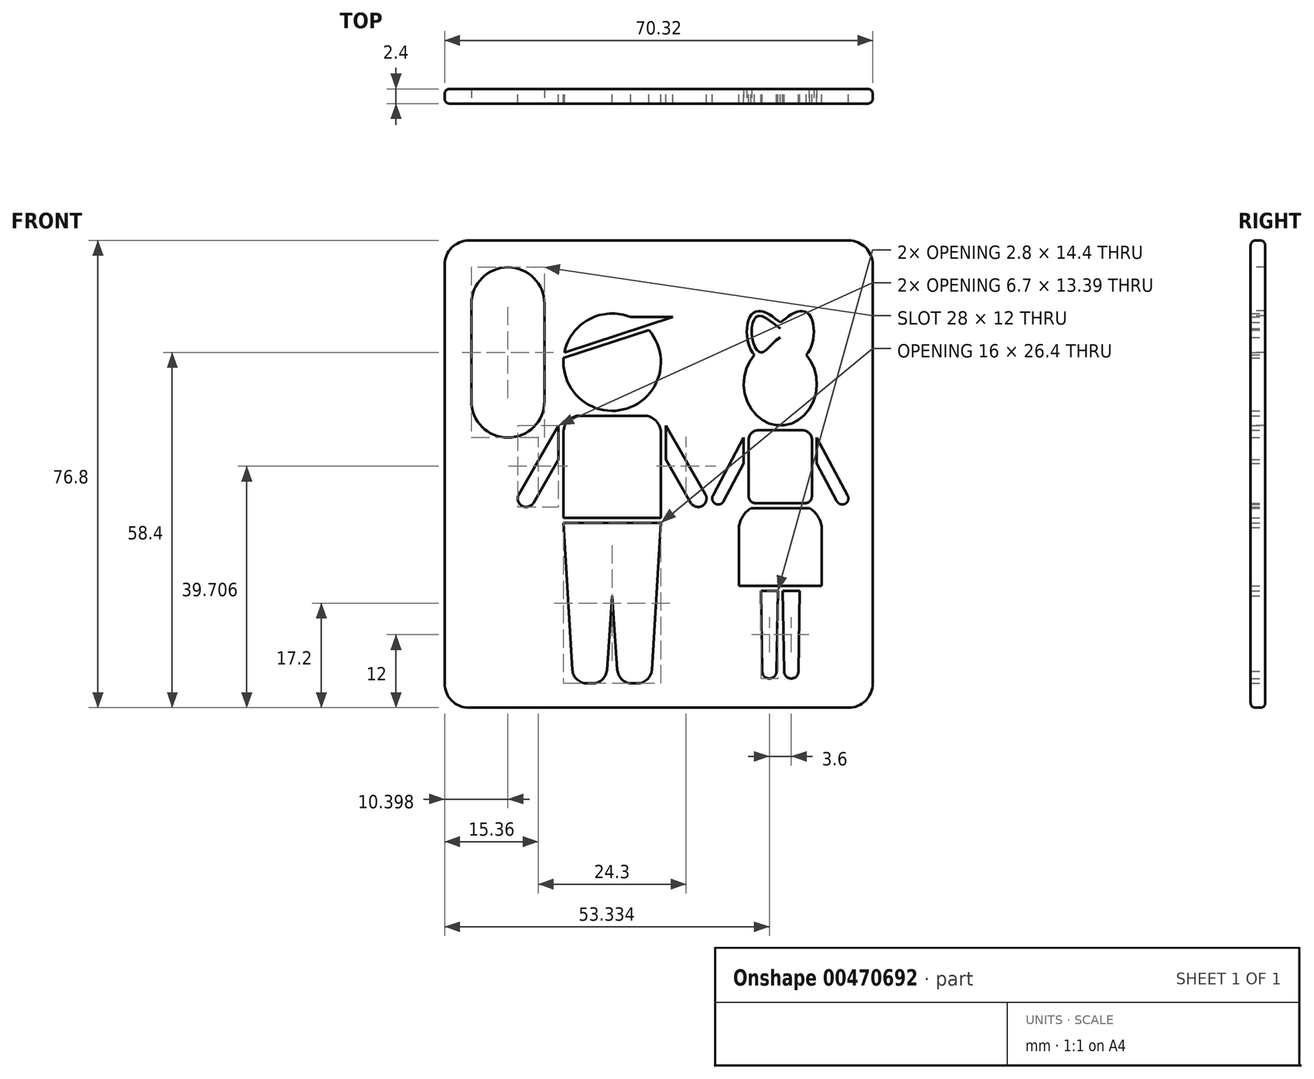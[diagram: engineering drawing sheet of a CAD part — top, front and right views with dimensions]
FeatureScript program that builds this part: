
annotation { "Feature Type Name" : "Feature", "Feature Type Description" : "" }
export const myFeature = defineFeature(function(context is Context, id is Id, definition is map)
    precondition{}
    {
        {
            var Q0;
            Q0=qCreatedBy(makeId("Front.planeOp"),FACE);
            var sketch = newSketch(context, id + "F0", { "sketchPlane" : qUnion([Q0])});
            skLineSegment(sketch, "E0", {"start": v(-25, 66) * mm, "end": v(-25, 0) * mm, "construction": true});
            skArc(sketch, "E1", {"start": v(-21.19, 75.25) * mm, "mid": v(-29.7, 74.83) * mm, "end": v(-34.8, 68) * mm});
            skLineSegment(sketch, "E2.bottom", {"start": v(-31.5, 55) * mm, "end": v(-18.5, 55) * mm});
            skLineSegment(sketch, "E2.top", {"start": v(-35, 34) * mm, "end": v(-15, 34) * mm});
            skLineSegment(sketch, "E2.left", {"start": v(-35, 51.5) * mm, "end": v(-35, 34) * mm});
            skLineSegment(sketch, "E2.right", {"start": v(-15, 51.5) * mm, "end": v(-15, 34) * mm});
            skPoint(sketch, "E2.middle", {"position": v(-25, 44.5) * mm});
            skPoint(sketch, "E3.visualSharp", {"position": v(-15, 55) * mm});
            skArc(sketch, "E3.filletArc", {"start": v(-15, 51.5) * mm, "mid": v(-16.03, 53.97) * mm, "end": v(-18.5, 55) * mm});
            skPoint(sketch, "E4.visualSharp", {"position": v(-35, 55) * mm});
            skArc(sketch, "E4.filletArc", {"start": v(-31.5, 55) * mm, "mid": v(-33.97, 53.97) * mm, "end": v(-35, 51.5) * mm});
            skLineSegment(sketch, "E5", {"start": v(-35, 66) * mm, "end": v(-15, 66) * mm, "construction": true});
            skLineSegment(sketch, "E6", {"start": v(-34.8, 68) * mm, "end": v(-12.5, 75.25) * mm});
            skLineSegment(sketch, "E7", {"start": v(-12.5, 75.25) * mm, "end": v(-21.19, 75.25) * mm});
            skLineSegment(sketch, "E8", {"start": v(-34.96, 66.9) * mm, "end": v(-17.47, 72.58) * mm});
            skLineSegment(sketch, "E9", {"start": v(-35, 33) * mm, "end": v(-15, 33) * mm});
            skLineSegment(sketch, "E10", {"start": v(-35, 33) * mm, "end": v(-33.15, 2.82) * mm});
            skLineSegment(sketch, "E11", {"start": v(-30.16, 0) * mm, "end": v(-29.06, 0) * mm});
            skLineSegment(sketch, "E12", {"start": v(-26.06, 2.8) * mm, "end": v(-25, 18) * mm});
            skPoint(sketch, "E13.visualSharp", {"position": v(-26.26, 0) * mm});
            skArc(sketch, "E13.filletArc", {"start": v(-29.06, 0) * mm, "mid": v(-27.01, 0.8) * mm, "end": v(-26.06, 2.8) * mm});
            skPoint(sketch, "E14.visualSharp", {"position": v(-32.98, 0) * mm});
            skArc(sketch, "E14.filletArc", {"start": v(-33.15, 2.82) * mm, "mid": v(-32.22, 0.81) * mm, "end": v(-30.16, 0) * mm});
            skLineSegment(sketch, "E15.MirrorCS", {"start": v(-15, 33) * mm, "end": v(-16.85, 2.82) * mm});
            skArc(sketch, "E16.MirrorCS", {"start": v(-16.85, 2.82) * mm, "mid": v(-17.78, 0.81) * mm, "end": v(-19.84, 0) * mm});
            skLineSegment(sketch, "E17.MirrorCS", {"start": v(-19.84, 0) * mm, "end": v(-20.94, 0) * mm});
            skArc(sketch, "E18.MirrorCS", {"start": v(-20.94, 0) * mm, "mid": v(-22.99, 0.8) * mm, "end": v(-23.94, 2.8) * mm});
            skLineSegment(sketch, "E19.MirrorCS", {"start": v(-23.94, 2.8) * mm, "end": v(-25, 18) * mm});
            skLineSegment(sketch, "E20", {"start": v(-36, 53) * mm, "end": v(-44.16, 38.88) * mm});
            skLineSegment(sketch, "E21", {"start": v(-41.12, 37.13) * mm, "end": v(-36, 46) * mm});
            skLineSegment(sketch, "E22", {"start": v(-36, 46) * mm, "end": v(-36, 53) * mm});
            skArc(sketch, "E23", {"start": v(-44.16, 38.88) * mm, "mid": v(-43.51, 36.48) * mm, "end": v(-41.12, 37.13) * mm});
            skLineSegment(sketch, "E24.MirrorCS", {"start": v(-14, 53) * mm, "end": v(-5.84, 38.88) * mm});
            skLineSegment(sketch, "E25.MirrorCS", {"start": v(-8.88, 37.13) * mm, "end": v(-14, 46) * mm});
            skLineSegment(sketch, "E26.MirrorCS", {"start": v(-14, 46) * mm, "end": v(-14, 53) * mm});
            skArc(sketch, "E27.MirrorCS", {"start": v(-5.84, 38.88) * mm, "mid": v(-6.49, 36.48) * mm, "end": v(-8.88, 37.13) * mm});
            skArc(sketch, "E28.trimOffspring", {"start": v(-34.96, 66.9) * mm, "mid": v(-21.9, 56.49) * mm, "end": v(-17.47, 72.58) * mm});
            skLineSegment(sketch, "E29", {"start": v(9.53, 1) * mm, "end": v(9.53, 61.5) * mm, "construction": true});
            skLineSegment(sketch, "E30.bottom", {"start": v(5.53, 19) * mm, "end": v(9.03, 19) * mm});
            skLineSegment(sketch, "E30.top", {"start": v(5.82, 2.46) * mm, "end": v(8.74, 2.46) * mm, "construction": true});
            skLineSegment(sketch, "E30.left", {"start": v(5.53, 19) * mm, "end": v(5.82, 2.46) * mm});
            skLineSegment(sketch, "E30.right", {"start": v(9.03, 19) * mm, "end": v(8.74, 2.46) * mm});
            skArc(sketch, "E31", {"start": v(8.74, 2.46) * mm, "mid": v(7.28, 1) * mm, "end": v(5.82, 2.46) * mm});
            skLineSegment(sketch, "E32", {"start": v(5.17, 1) * mm, "end": v(7.83, 1) * mm, "construction": true});
            skLineSegment(sketch, "E33", {"start": v(9.53, 20) * mm, "end": v(1.03, 20) * mm});
            skLineSegment(sketch, "E34", {"start": v(1.03, 20) * mm, "end": v(1.03, 32) * mm});
            skLineSegment(sketch, "E35", {"start": v(9.53, 36) * mm, "end": v(3.53, 36) * mm});
            skArc(sketch, "E36", {"start": v(3.53, 36) * mm, "mid": v(1.8, 34.3) * mm, "end": v(1.03, 32) * mm});
            skLineSegment(sketch, "E37.MirrorCS", {"start": v(13.24, 2.46) * mm, "end": v(10.32, 2.46) * mm, "construction": true});
            skArc(sketch, "E38.MirrorCS", {"start": v(10.32, 2.46) * mm, "mid": v(11.78, 1) * mm, "end": v(13.24, 2.46) * mm});
            skLineSegment(sketch, "E39.MirrorCS", {"start": v(10.03, 19) * mm, "end": v(10.32, 2.46) * mm});
            skLineSegment(sketch, "E40.MirrorCS", {"start": v(13.53, 19) * mm, "end": v(10.03, 19) * mm});
            skLineSegment(sketch, "E41.MirrorCS", {"start": v(13.53, 19) * mm, "end": v(13.24, 2.46) * mm});
            skLineSegment(sketch, "E42.MirrorCS", {"start": v(9.53, 36) * mm, "end": v(15.53, 36) * mm});
            skArc(sketch, "E43.MirrorCS", {"start": v(15.53, 36) * mm, "mid": v(17.26, 34.3) * mm, "end": v(18.03, 32) * mm});
            skLineSegment(sketch, "E44.MirrorCS", {"start": v(18.03, 20) * mm, "end": v(18.03, 32) * mm});
            skLineSegment(sketch, "E45.MirrorCS", {"start": v(9.53, 20) * mm, "end": v(18.03, 20) * mm});
            skLineSegment(sketch, "E46", {"start": v(9.53, 37) * mm, "end": v(4.53, 37) * mm});
            skLineSegment(sketch, "E47", {"start": v(3.03, 38.5) * mm, "end": v(3.03, 50) * mm});
            skLineSegment(sketch, "E48", {"start": v(5.03, 52) * mm, "end": v(9.53, 52) * mm});
            skPoint(sketch, "E49.visualSharp", {"position": v(3.03, 37) * mm});
            skArc(sketch, "E49.filletArc", {"start": v(3.03, 38.5) * mm, "mid": v(3.47, 37.44) * mm, "end": v(4.53, 37) * mm});
            skPoint(sketch, "E50.visualSharp", {"position": v(3.03, 52) * mm});
            skArc(sketch, "E50.filletArc", {"start": v(5.03, 52) * mm, "mid": v(3.62, 51.41) * mm, "end": v(3.03, 50) * mm});
            skLineSegment(sketch, "E51.MirrorCS", {"start": v(14.03, 52) * mm, "end": v(9.53, 52) * mm});
            skArc(sketch, "E52.MirrorCS", {"start": v(14.03, 52) * mm, "mid": v(15.44, 51.41) * mm, "end": v(16.03, 50) * mm});
            skLineSegment(sketch, "E53.MirrorCS", {"start": v(16.03, 38.5) * mm, "end": v(16.03, 50) * mm});
            skArc(sketch, "E54.MirrorCS", {"start": v(16.03, 38.5) * mm, "mid": v(15.6, 37.44) * mm, "end": v(14.53, 37) * mm});
            skLineSegment(sketch, "E55.MirrorCS", {"start": v(9.53, 37) * mm, "end": v(14.53, 37) * mm});
            skLineSegment(sketch, "E56", {"start": v(2.03, 50.5) * mm, "end": v(2.03, 45.17) * mm});
            skLineSegment(sketch, "E57", {"start": v(2.03, 45.17) * mm, "end": v(-2.1, 37.41) * mm});
            skLineSegment(sketch, "E58", {"start": v(-2.1, 37.41) * mm, "end": v(-4.3, 38.59) * mm, "construction": true});
            skLineSegment(sketch, "E59", {"start": v(-4.3, 38.59) * mm, "end": v(2.03, 50.5) * mm});
            skArc(sketch, "E60", {"start": v(-2.1, 37.41) * mm, "mid": v(-3.79, 36.9) * mm, "end": v(-4.3, 38.59) * mm});
            skLineSegment(sketch, "E61.MirrorCS", {"start": v(17.03, 50.5) * mm, "end": v(17.03, 45.17) * mm});
            skLineSegment(sketch, "E62.MirrorCS", {"start": v(23.36, 38.59) * mm, "end": v(17.03, 50.5) * mm});
            skLineSegment(sketch, "E63.MirrorCS", {"start": v(17.03, 45.17) * mm, "end": v(21.16, 37.41) * mm});
            skArc(sketch, "E64.MirrorCS", {"start": v(21.16, 37.41) * mm, "mid": v(22.85, 36.9) * mm, "end": v(23.36, 38.59) * mm});
            skEllipticalArc(sketch, "E65", {});
            skPoint(sketch, "E66.4.internal.snap0", {"position": v(9.53, 70) * mm});
            skFitSpline(sketch, "E66", {"points": [v(9.53, 71.09) * mm, v(5.61, 67.97) * mm, v(3.73, 71.18) * mm, v(5.07, 75.5) * mm, v(9.53, 72.94) * mm], "startDerivative": vector(-20.3, -12.18) * mm, "endDerivative": vector(11.91, -6.98) * mm});
            skFitSpline(sketch, "E67.MirrorCS", {"points": [v(9.53, 71.09) * mm, v(13.45, 67.97) * mm, v(15.33, 71.18) * mm, v(13.98, 75.5) * mm, v(9.53, 72.94) * mm], "startDerivative": vector(20.3, -12.18) * mm, "endDerivative": vector(-11.91, -6.98) * mm});
            skFitSpline(sketch, "E68.0", {"points": [v(10.04, 70.23) * mm, v(9.7, 70.02) * mm, v(9.2, 69.62) * mm, v(8.55, 69) * mm, v(8.08, 68.52) * mm, v(7.62, 68.05) * mm, v(7.15, 67.62) * mm, v(6.72, 67.3) * mm, v(6.3, 67.1) * mm, v(6, 67) * mm, v(5.73, 66.97) * mm, v(5.44, 66.96) * mm, v(5.1, 67.02) * mm, v(4.74, 67.17) * mm, v(4.33, 67.43) * mm, v(3.92, 67.85) * mm, v(3.54, 68.43) * mm, v(3.23, 69.08) * mm, v(2.99, 69.8) * mm, v(2.8, 70.58) * mm, v(2.7, 71.4) * mm, v(2.65, 72.22) * mm, v(2.68, 73.04) * mm, v(2.79, 73.84) * mm, v(2.98, 74.6) * mm, v(3.28, 75.3) * mm, v(3.66, 75.82) * mm, v(4.08, 76.17) * mm, v(4.46, 76.38) * mm, v(4.83, 76.48) * mm, v(5.12, 76.51) * mm, v(5.4, 76.51) * mm, v(5.75, 76.47) * mm, v(6.25, 76.33) * mm, v(6.82, 76.07) * mm, v(7.48, 75.68) * mm, v(8.11, 75.23) * mm, v(8.7, 74.78) * mm, v(9.25, 74.36) * mm, v(9.72, 74) * mm, v(9.95, 73.85) * mm, v(10.04, 73.8) * mm]});
            skFitSpline(sketch, "E69.0", {"points": [v(9.02, 70.23) * mm, v(9.36, 70.02) * mm, v(9.87, 69.62) * mm, v(10.5, 69) * mm, v(10.98, 68.52) * mm, v(11.44, 68.05) * mm, v(11.9, 67.62) * mm, v(12.34, 67.3) * mm, v(12.76, 67.1) * mm, v(13.06, 67) * mm, v(13.33, 66.97) * mm, v(13.61, 66.96) * mm, v(13.95, 67.02) * mm, v(14.32, 67.17) * mm, v(14.73, 67.43) * mm, v(15.14, 67.85) * mm, v(15.52, 68.43) * mm, v(15.83, 69.08) * mm, v(16.07, 69.8) * mm, v(16.25, 70.58) * mm, v(16.37, 71.4) * mm, v(16.4, 72.22) * mm, v(16.38, 73.04) * mm, v(16.27, 73.84) * mm, v(16.08, 74.6) * mm, v(15.78, 75.3) * mm, v(15.4, 75.82) * mm, v(14.98, 76.17) * mm, v(14.6, 76.38) * mm, v(14.23, 76.48) * mm, v(13.94, 76.51) * mm, v(13.65, 76.51) * mm, v(13.31, 76.47) * mm, v(12.81, 76.33) * mm, v(12.23, 76.07) * mm, v(11.58, 75.68) * mm, v(10.95, 75.23) * mm, v(10.35, 74.78) * mm, v(9.8, 74.36) * mm, v(9.34, 74) * mm, v(9.1, 73.85) * mm, v(9.02, 73.8) * mm]});
            const initialGuessF0  = {"E65": [0.009529412724077696, 0.0615, 0, -1, 0.0085, 0.0075, 3.9233208754425206, 2.359864431737064]};
            skSetInitialGuess(sketch, initialGuessF0);
            skSolve(sketch);
        }
        {
            var Q0;
            Q0=qCreatedBy(makeId("Front.planeOp"),FACE);
            var sketch = newSketch(context, id + "F1", { "sketchPlane" : qUnion([Q0])});
            skLineSegment(sketch, "E70.bottom", {"start": v(-59.39, 91) * mm, "end": v(28.51, 91) * mm});
            skLineSegment(sketch, "E70.top", {"start": v(-59.39, -5) * mm, "end": v(28.51, -5) * mm});
            skLineSegment(sketch, "E70.left", {"start": v(-59.39, 91) * mm, "end": v(-59.39, -5) * mm});
            skLineSegment(sketch, "E70.right", {"start": v(28.51, 91) * mm, "end": v(28.51, -5) * mm});
            skArc(sketch, "E71.0", {"start": v(-44.16, 38.88) * mm, "mid": v(-43.51, 36.48) * mm, "end": v(-41.12, 37.13) * mm, "construction": true});
            skArc(sketch, "E72.0", {"start": v(-21.19, 75.25) * mm, "mid": v(-29.7, 74.83) * mm, "end": v(-34.8, 68) * mm, "construction": true});
            skArc(sketch, "E73.0", {"start": v(21.16, 37.41) * mm, "mid": v(22.85, 36.9) * mm, "end": v(23.36, 38.59) * mm, "construction": true});
            skSolve(sketch);
        }
        {
            var Q0;
            Q0=qSketchRegion(id+"F1",true);
            extrude(context, id + "F2", {"entities" : qUnion([Q0]), "depth" : 3 * mm});
        }
        {
            var Q0;
            Q0=qSketchRegion(id+"F0",true);
            extrude(context, id + "F3", {"entities" : qUnion([Q0]), "operationType" : NewBodyOperationType.REMOVE, "endBound" : BoundingType.THROUGH_ALL, "depth" : 25 * mm});
        }
        {
            var Q0;
            Q0=makeQuery(id+"F2.opExtrude","CAP_FACE",FACE,{"disambiguationData":[OSD([sQuery(id+"F1.wireOp",EDGE,"E70.bottom"),sQuery(id+"F1.wireOp",EDGE,"E70.top"),sQuery(id+"F1.wireOp",EDGE,"E70.left"),sQuery(id+"F1.wireOp",EDGE,"E70.right")])],"isStart":false});
            var sketch = newSketch(context, id + "F4", { "sketchPlane" : qUnion([Q0])});
            skArc(sketch, "E74", {"start": v(-38.89, 78) * mm, "mid": v(-46.39, 85.5) * mm, "end": v(-53.89, 78) * mm});
            skArc(sketch, "E75", {"start": v(-53.89, 58) * mm, "mid": v(-46.39, 50.5) * mm, "end": v(-38.89, 58) * mm});
            skLineSegment(sketch, "E76", {"start": v(-53.89, 78) * mm, "end": v(-53.89, 58) * mm});
            skLineSegment(sketch, "E77", {"start": v(-38.89, 58) * mm, "end": v(-38.89, 78) * mm});
            skSolve(sketch);
        }
        {
            var Q0;
            Q0=makeQuery(id+"F4.imprint","IMPRINT",FACE,{"disambiguationData":[TD([[makeQuery(id+"F4.imprint","IMPRINT",EDGE,{"derivedFrom":sQuery(id+"F4.wireOp",EDGE,"E74")}),1.0]])]});
            extrude(context, id + "F5", {"entities" : qUnion([Q0]), "operationType" : NewBodyOperationType.REMOVE, "endBound" : BoundingType.UP_TO_NEXT, "oppositeDirection" : true, "depth" : 25 * mm, "offsetDistance" : 25 * mm});
        }
        {
            var Q0;
            Q0=makeQuery(id+"F2.opExtrude","SWEPT_EDGE",EDGE,{"disambiguationData":[OSD([sQuery(id+"F1.wireOp",EDGE,"E70.bottom"),sQuery(id+"F1.wireOp",EDGE,"E70.right")])]});
            var Q1;
            Q1=makeQuery(id+"F2.opExtrude","SWEPT_EDGE",EDGE,{"disambiguationData":[OSD([sQuery(id+"F1.wireOp",EDGE,"E70.top"),sQuery(id+"F1.wireOp",EDGE,"E70.right")])]});
            var Q2;
            Q2=makeQuery(id+"F2.opExtrude","SWEPT_EDGE",EDGE,{"disambiguationData":[OSD([sQuery(id+"F1.wireOp",EDGE,"E70.top"),sQuery(id+"F1.wireOp",EDGE,"E70.left")])]});
            var Q3;
            Q3=makeQuery(id+"F2.opExtrude","SWEPT_EDGE",EDGE,{"disambiguationData":[OSD([sQuery(id+"F1.wireOp",EDGE,"E70.bottom"),sQuery(id+"F1.wireOp",EDGE,"E70.left")])]});
            fillet(context, id + "F6", {"entities" : qUnion([Q0, Q1, Q2, Q3]), "radius" : 5 * mm, "tangentPropagation" : true, "allowEdgeOverflow" : false});
        }
        {
            var Q0;
            Q0=makeQuery(id+"F2.opExtrude","CAP_EDGE",EDGE,{"disambiguationData":[OSD([sQuery(id+"F1.wireOp",EDGE,"E70.bottom")])],"isStart":false});
            var Q1;
            Q1=makeQuery(id+"F2.opExtrude","CAP_EDGE",EDGE,{"disambiguationData":[OSD([sQuery(id+"F1.wireOp",EDGE,"E70.bottom")])],"isStart":true});
            fillet(context, id + "F7", {"entities" : qUnion([Q0, Q1]), "radius" : 1 * mm, "tangentPropagation" : true, "allowEdgeOverflow" : false});
        }
        {
            var Q0;
            Q0=makeQuery(id+"F2.opExtrude","SWEPT_BODY",BODY,{"disambiguationData":[OSD([sQuery(id+"F1.wireOp",EDGE,"E70.bottom"),sQuery(id+"F1.wireOp",EDGE,"E70.top"),sQuery(id+"F1.wireOp",EDGE,"E70.left"),sQuery(id+"F1.wireOp",EDGE,"E70.right")])]});
            var Q1;
            Q1=qCreatedBy(makeId("Origin.pointOp"),VERTEX);
            transform(context, id + "F8", {"entities" : qUnion([Q0]), "transformType" : TransformType.SCALE_UNIFORMLY, "scale" : 0.8, "scalePoint" : qUnion([Q1]), "makeCopy" : false});
        }
    });
